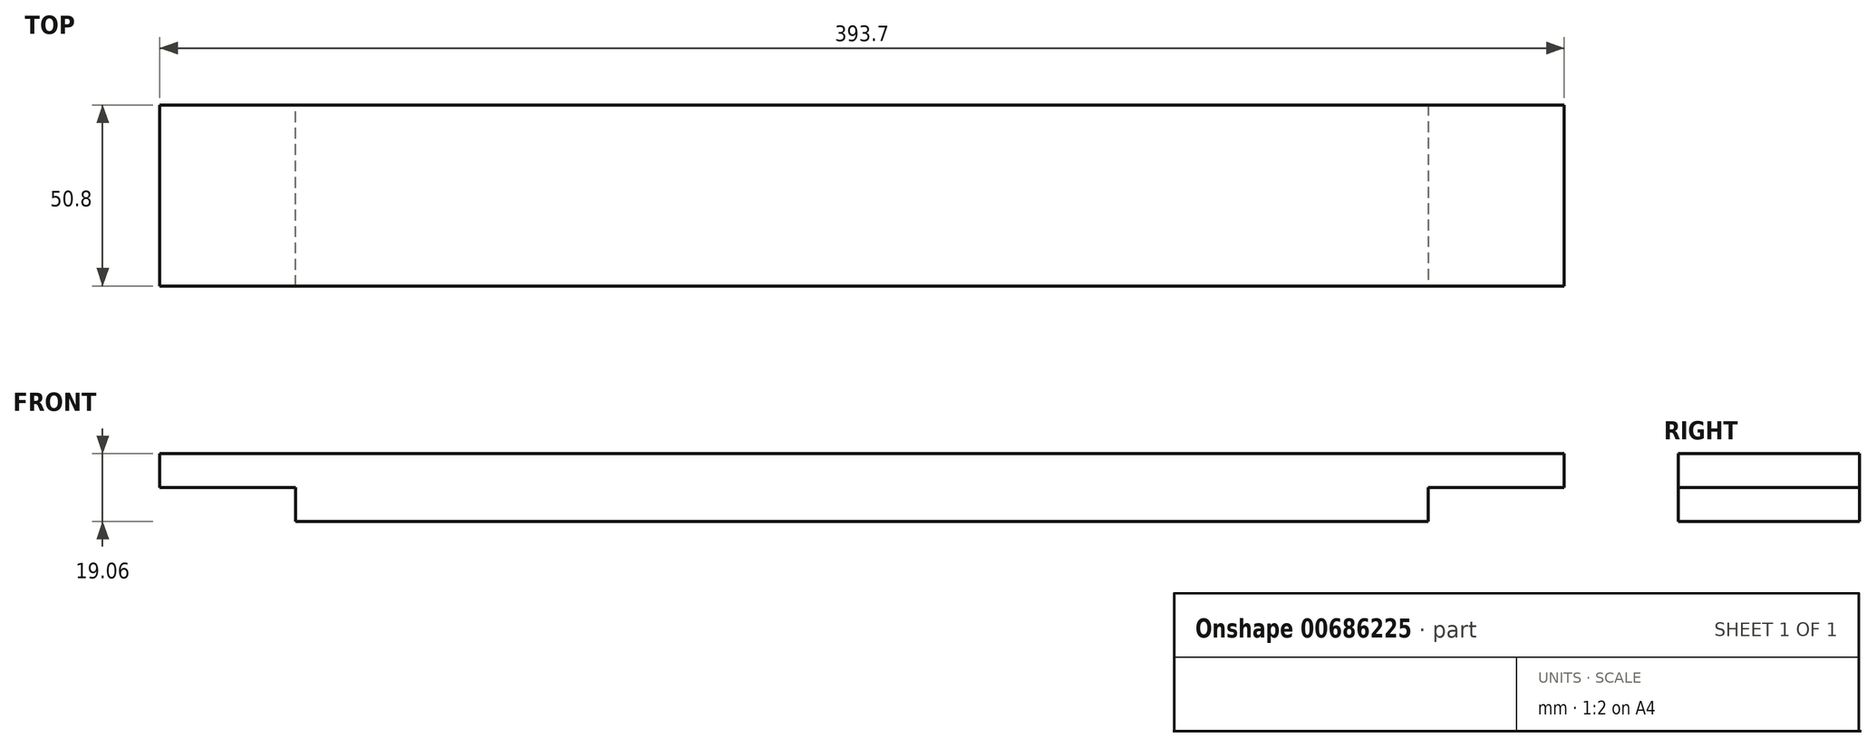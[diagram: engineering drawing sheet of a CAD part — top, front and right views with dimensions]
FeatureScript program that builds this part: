
annotation { "Feature Type Name" : "Feature", "Feature Type Description" : "" }
export const myFeature = defineFeature(function(context is Context, id is Id, definition is map)
    precondition{}
    {
        {
            var Q0;
            Q0=qCreatedBy(makeId("Top.planeOp"),FACE);
            var sketch = newSketch(context, id + "F0", { "sketchPlane" : qUnion([Q0])});
            skLineSegment(sketch, "E0.bottom", {"start": v(-196.85, 25.4) * mm, "end": v(196.85, 25.4) * mm});
            skLineSegment(sketch, "E0.top", {"start": v(-196.85, -25.4) * mm, "end": v(196.85, -25.4) * mm});
            skLineSegment(sketch, "E0.left", {"start": v(-196.85, 25.4) * mm, "end": v(-196.85, -25.4) * mm});
            skLineSegment(sketch, "E0.right", {"start": v(196.85, 25.4) * mm, "end": v(196.85, -25.4) * mm});
            skPoint(sketch, "E0.middle", {"position": v(0, 0) * mm});
            skSolve(sketch);
        }
        {
            var Q0;
            Q0=qSketchRegion(id+"F0",true);
            extrude(context, id + "F1", {"entities" : qUnion([Q0]), "endBound" : BoundingType.SYMMETRIC, "depth" : 19.05 * mm, "offsetDistance" : 25.4 * mm});
        }
        {
            var Q0;
            Q0=qCreatedBy(makeId("Top.planeOp"),FACE);
            var sketch = newSketch(context, id + "F2", { "sketchPlane" : qUnion([Q0])});
            skLineSegment(sketch, "E1.bottom", {"start": v(-196.85, 25.4) * mm, "end": v(-158.75, 25.4) * mm});
            skLineSegment(sketch, "E1.top", {"start": v(-196.85, -25.4) * mm, "end": v(-158.75, -25.4) * mm});
            skLineSegment(sketch, "E1.left", {"start": v(-196.85, -25.4) * mm, "end": v(-196.85, 25.4) * mm});
            skLineSegment(sketch, "E1.right", {"start": v(-158.75, -25.4) * mm, "end": v(-158.75, 25.4) * mm});
            skLineSegment(sketch, "E2.bottom", {"start": v(158.75, -25.4) * mm, "end": v(196.85, -25.4) * mm});
            skLineSegment(sketch, "E2.top", {"start": v(158.75, 25.4) * mm, "end": v(196.85, 25.4) * mm});
            skLineSegment(sketch, "E2.left", {"start": v(158.75, 25.4) * mm, "end": v(158.75, -25.4) * mm});
            skLineSegment(sketch, "E2.right", {"start": v(196.85, 25.4) * mm, "end": v(196.85, -25.4) * mm});
            skSolve(sketch);
        }
        {
            var Q0;
            Q0 = qSketchRegion(id + "F2", true);
            extrude(context, id + "F3", {"entities" : qUnion([Q0]), "operationType" : NewBodyOperationType.REMOVE, "endBound" : BoundingType.THROUGH_ALL, "oppositeDirection" : true, "depth" : 6.35 * mm, "offsetDistance" : 25.4 * mm});
        }
    });
